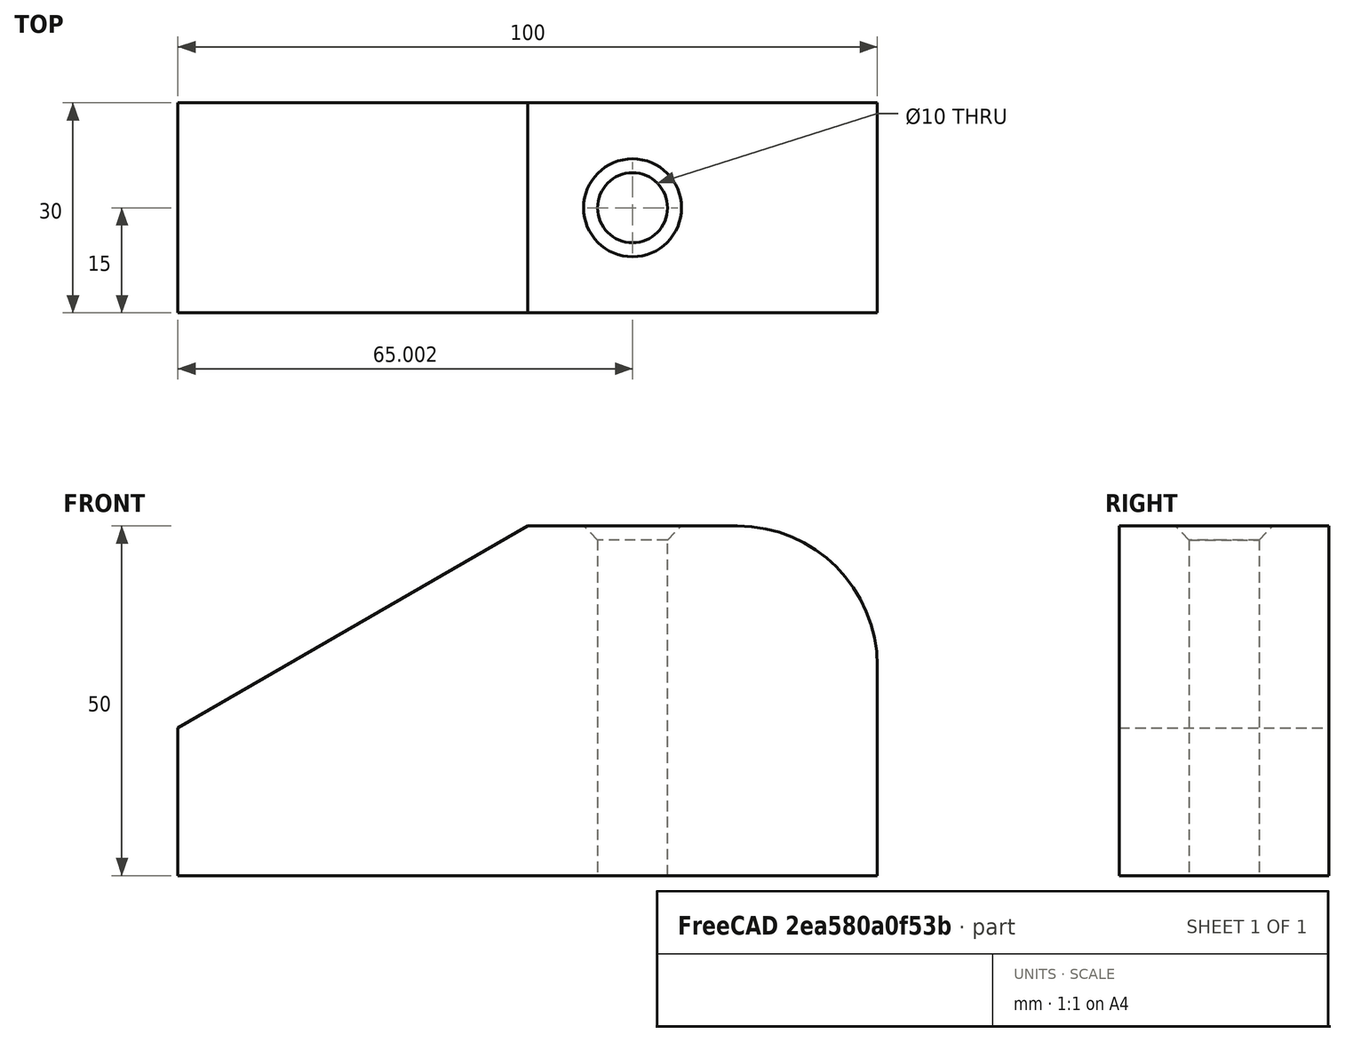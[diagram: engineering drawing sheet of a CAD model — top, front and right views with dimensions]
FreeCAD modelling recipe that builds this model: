
FCSTD DOCUMENT  (FreeCAD 0.20R29410 (Git))
Label: Creating a simple part with Part WB_Draft_WB_Locate_Hole
License: All rights reserved
LicenseURL: http://en.wikipedia.org/wiki/All_rights_reserved
objects: Part::Cut×3, Part::Box×2, Part::Fillet×1, Part::Cylinder×1, Part::Cone×1
note: 8 computed .brp shape members not serialized (recipe doc carries the construction recipe); baked Part::Feature solids carry a one-line shape summary decoded from their .brp

FEATURE [Part::Box] Box  label="Cube"
  AttacherType = Attacher::AttachEngine3D
  Height = 50
  Length = 100
  Width = 30
FEATURE [Part::Fillet] Fillet
  Base = -> Box
  Edges = 1 edges r=20: [Edge6]
FEATURE [Part::Box] Box001  label="Cube001"
  AttacherType = Attacher::AttachEngine3D
  Height = 30
  Length = 60
  Placement = pos=(0,0,21.13) rot=(0,1,0;-0.523599rad)
  Width = 30
FEATURE [Part::Cut] Cut
  Base = -> Fillet
  Tool = -> Box001
FEATURE [Part::Cylinder] Cylinder
  Angle = 360
  AttacherType = Attacher::AttachEngine3D
  FirstAngle = 0
  Height = 50
  Placement = pos=(65.0022,15,0) rot=(0,0,1;0rad)
  Radius = 5
  SecondAngle = 0
FEATURE [Part::Cut] Cut001
  Base = -> Cut
  Tool = -> Cylinder
FEATURE [Part::Cone] Cone
  Angle = 360
  AttacherType = Attacher::AttachEngine3D
  Height = 7
  Placement = pos=(65.0022,15,43) rot=(0,0,1;0rad)
  Radius1 = 0
  Radius2 = 7
FEATURE [Part::Cut] Cut002
  Base = -> Cut001
  Tool = -> Cone
